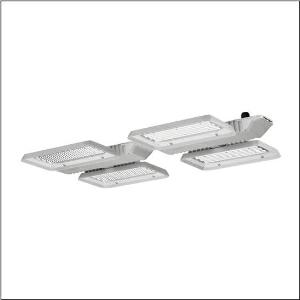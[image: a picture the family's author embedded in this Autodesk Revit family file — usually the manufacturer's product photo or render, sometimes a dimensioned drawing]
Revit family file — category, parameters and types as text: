
# Revit family: highbay_11_51hla2d24mcad
name_source: partatom
category: Lighting Fixtures
units: mm (PartAtom-declared; Revit-internal decimal feet)

## family parameters
Cut with Voids When Loaded = No
Host = Face
Light Source = No
Part Type = Normal
Room Calculation Point = No
Round Connector Dimension = Use Diameter
Shared = No

## types (1)
- --- (1 x LED, 4320 lm, 28.2 W, 4000K)
    Apparent Load = 28 VA
    CIE Flux Codes = 89 96 99 100 100
    Color Rendering = 80
    Color Temperature = 4000K
    Default Elevation = 1800 mm
    Description = Highbay 11, LED high bay luminaire, primary light control with lens, of PMMA, light emission: direct distribution, primary light characteristic: symmetric, installation type: suspended mounting, surface-mounted, for 2x 2x LED, rated luminous flux: 28.800lm, luminous efficacy: 177lm/W, light colour: 840, colour temperature: 4000K, control gear: ECG DALI, with terminal, 5-pole, max. 2.5mm², mains connection: 230..240V, AC/DC, 50/60Hz, rated input power: 162W, LED unit, of diecast aluminium, bead blasted, unplated, silver, length: 940mm, width: 500mm, height: 65mm, housing, of diecast aluminium, bead blasted, uncoated, silver, protection rating (complete): IP65, insulation class (complete): insulation class I (protective earthing), certification: CE, UKCA, protection symbol: D, impact resistance: IK08 with glass or PC cover, permissible operating ambient temperature: -35..+55°C, standard: EN 60598-2-22, reducing of maximum allowable ambient temperature of 5°C with ceiling mounting, corresponds to IFS (International Featured Standards) requirements for safety and quality in the food industry, packaging unit: 1 piece
    Height = 95 mm
    Lamp = 1 x LED
    Lamp Light Flux = 4320 lm
    Lamp Power = 28.2 W
    Lamp count = 1
    Length = 939 mm
    Luminous efficacy = 153 lm/W
    Manufacturer = Siteco
    ModVariant = No
    Model = 51HLA2D24MCAD
    Mounting Place = Ceiling
    Mounting Type = Pendant
    Number of Poles = 1
    OnlyDefault = Yes
    Power Factor = 1
    Product Name = Highbay 11
    Product group = LED high bay luminaire
    ProductGroupID = 903
    Protection Class = Protection class I
    Protection Degree = IP 65
    RLX_Detail_Level = 1
    RLX_Emergency_Light_Flux = 0 lm
    RLX_Emergency_Type = 0
    RLX_Emergency_Type_DB = No
    RlxData = <blob elided: 104525 chars, md5=111b7872>
    Socket = socket
    Standby Power = 0 W
    System Light Flux = 4320 lm
    System Power = 28 W
    Type Comments = : central accumulator DC – ECG emengency level 15%
    Type Image = l_1003428.jpg
    URL = http://relux.com
    VarID = @adj_152823
    Voltage = 0 V
    Weight = 0.00 kg
    Width = 501 mm

## geometry (parser evidence)
native form markers: Blend x4, Sweep x10
no freeform markers — native parametric forms only
